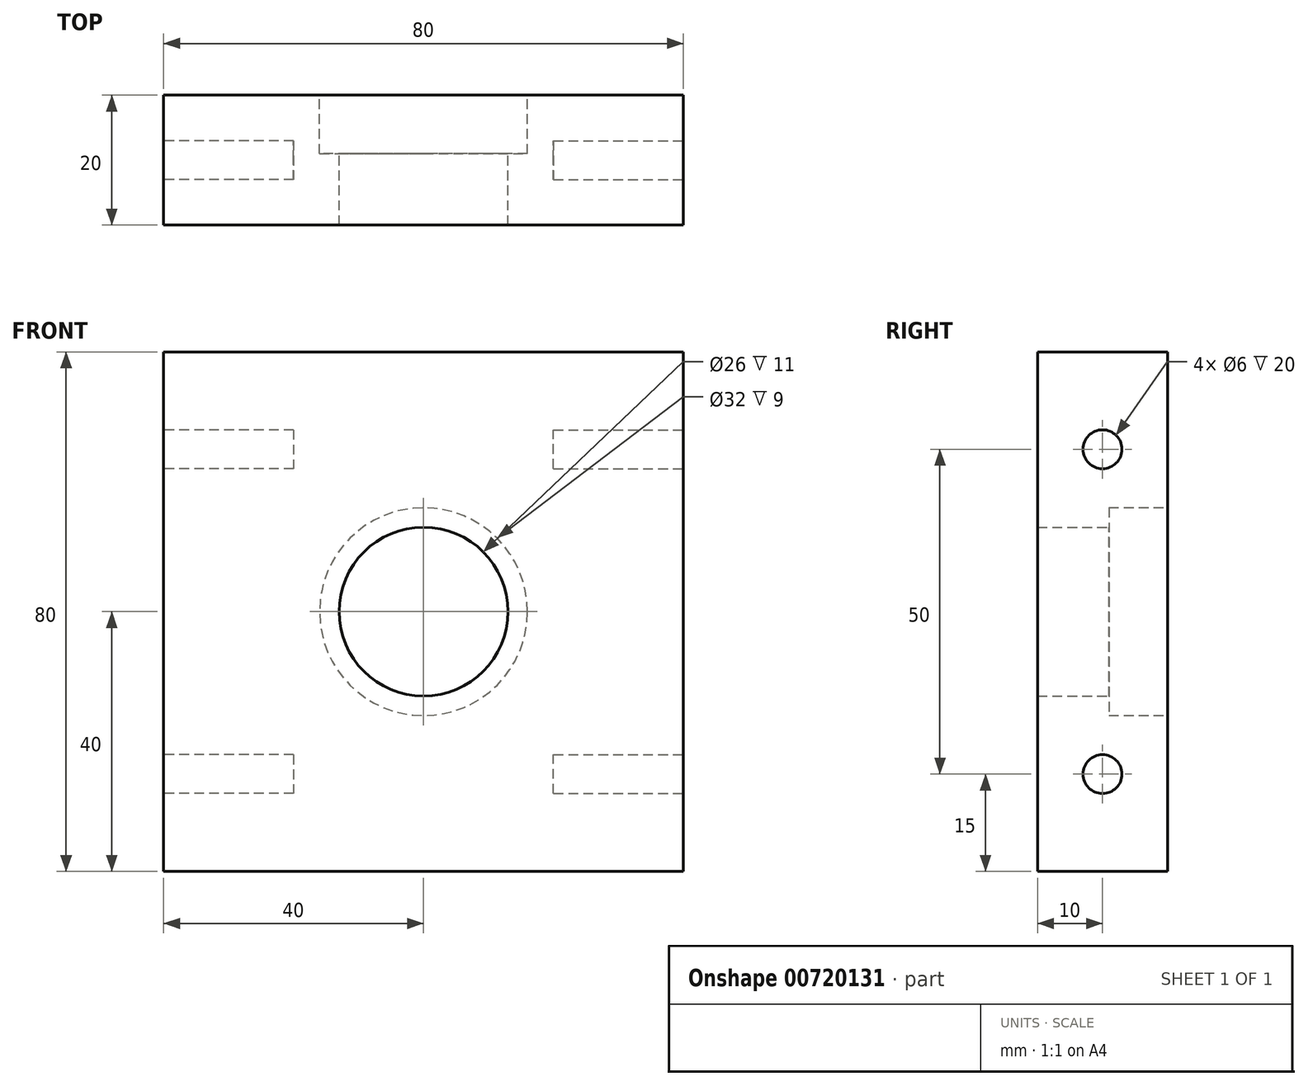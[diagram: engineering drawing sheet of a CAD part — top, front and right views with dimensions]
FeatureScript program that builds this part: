
annotation { "Feature Type Name" : "Feature", "Feature Type Description" : "" }
export const myFeature = defineFeature(function(context is Context, id is Id, definition is map)
    precondition{}
    {
        {
            var Q0;
            Q0=qCreatedBy(makeId("Front.planeOp"),FACE);
            var sketch = newSketch(context, id + "F0", { "sketchPlane" : qUnion([Q0])});
            skLineSegment(sketch, "E0.bottom", {"start": v(0, 0) * mm, "end": v(80, 0) * mm});
            skLineSegment(sketch, "E0.top", {"start": v(0, 80) * mm, "end": v(80, 80) * mm});
            skLineSegment(sketch, "E0.left", {"start": v(0, 0) * mm, "end": v(0, 80) * mm});
            skLineSegment(sketch, "E0.right", {"start": v(80, 0) * mm, "end": v(80, 80) * mm});
            skCircle(sketch, "E1", {"center": v(40, 40) * mm, "radius": 13 * mm});
            skPoint(sketch, "E1.centerSnap0", {"position": v(40, 80) * mm});
            skPoint(sketch, "E1.centerSnap1", {"position": v(0, 40) * mm});
            skSolve(sketch);
        }
        {
            var Q0;
            Q0=makeQuery(id+"F0.imprint","IMPRINT",FACE,{"disambiguationData":[TD([[makeQuery(id+"F0.imprint","IMPRINT",EDGE,{"derivedFrom":sQuery(id+"F0.wireOp",EDGE,"E0.bottom")}),1.0]])]});
            extrude(context, id + "F1", {"entities" : qUnion([Q0]), "depth" : 20 * mm, "offsetDistance" : 25 * mm});
        }
        {
            var Q0;
            Q0=makeQuery(id+"F1.opExtrude","CAP_FACE",FACE,{"disambiguationData":[OSD([sQuery(id+"F0.wireOp",EDGE,"E0.bottom"),sQuery(id+"F0.wireOp",EDGE,"E0.top"),sQuery(id+"F0.wireOp",EDGE,"E0.left"),sQuery(id+"F0.wireOp",EDGE,"E0.right"),sQuery(id+"F0.wireOp",EDGE,"E1")])],"isStart":true});
            var sketch = newSketch(context, id + "F2", { "sketchPlane" : qUnion([Q0])});
            skCircle(sketch, "E2", {"center": v(-40, 40) * mm, "radius": 16 * mm});
            skSolve(sketch);
        }
        {
            var Q0;
            Q0=makeQuery(id+"F2.imprint","IMPRINT",FACE,{"disambiguationData":[TD([[makeQuery(id+"F2.imprint","IMPRINT",EDGE,{"derivedFrom":sQuery(id+"F2.wireOp",EDGE,"E2")}),1.0]])]});
            extrude(context, id + "F3", {"entities" : qUnion([Q0]), "operationType" : NewBodyOperationType.REMOVE, "oppositeDirection" : true, "depth" : 9 * mm, "offsetDistance" : 25 * mm});
        }
        {
            var Q0;
            Q0=makeQuery(id+"F1.opExtrude","SWEPT_FACE",FACE,{"disambiguationData":[OSD([sQuery(id+"F0.wireOp",EDGE,"E0.right")])]});
            var sketch = newSketch(context, id + "F4", { "sketchPlane" : qUnion([Q0])});
            skCircle(sketch, "E3", {"center": v(-10, 65) * mm, "radius": 3 * mm});
            skPoint(sketch, "E3.centerSnap0", {"position": v(-10, 80) * mm});
            skCircle(sketch, "E4", {"center": v(-10, 15) * mm, "radius": 3 * mm});
            skSolve(sketch);
        }
        {
            var Q0;
            Q0 = qSketchRegion(id + "F4", true);
            extrude(context, id + "F5", {"entities" : qUnion([Q0]), "operationType" : NewBodyOperationType.REMOVE, "oppositeDirection" : true, "depth" : 20 * mm, "offsetDistance" : 25 * mm});
        }
        {
            var Q0;
            Q0=makeQuery(id+"F1.opExtrude","SWEPT_FACE",FACE,{"disambiguationData":[OSD([sQuery(id+"F0.wireOp",EDGE,"E0.left")])]});
            var sketch = newSketch(context, id + "F6", { "sketchPlane" : qUnion([Q0])});
            skCircle(sketch, "E5", {"center": v(10, 65) * mm, "radius": 3 * mm});
            skPoint(sketch, "E5.centerSnap0", {"position": v(10, 80) * mm});
            skCircle(sketch, "E6", {"center": v(10, 15) * mm, "radius": 3 * mm});
            skPoint(sketch, "E6.centerSnap0", {"position": v(10, 0) * mm});
            skSolve(sketch);
        }
        {
            var Q0;
            Q0=makeQuery(id+"F6.imprint","IMPRINT",FACE,{"disambiguationData":[TD([[makeQuery(id+"F6.imprint","IMPRINT",EDGE,{"derivedFrom":sQuery(id+"F6.wireOp",EDGE,"E5")}),1.0]])]});
            var Q1;
            Q1=makeQuery(id+"F6.imprint","IMPRINT",FACE,{"disambiguationData":[TD([[makeQuery(id+"F6.imprint","IMPRINT",EDGE,{"derivedFrom":sQuery(id+"F6.wireOp",EDGE,"E6")}),1.0]])]});
            extrude(context, id + "F7", {"entities" : qUnion([Q0, Q1]), "operationType" : NewBodyOperationType.REMOVE, "oppositeDirection" : true, "depth" : 20 * mm, "offsetDistance" : 25 * mm});
        }
    });
